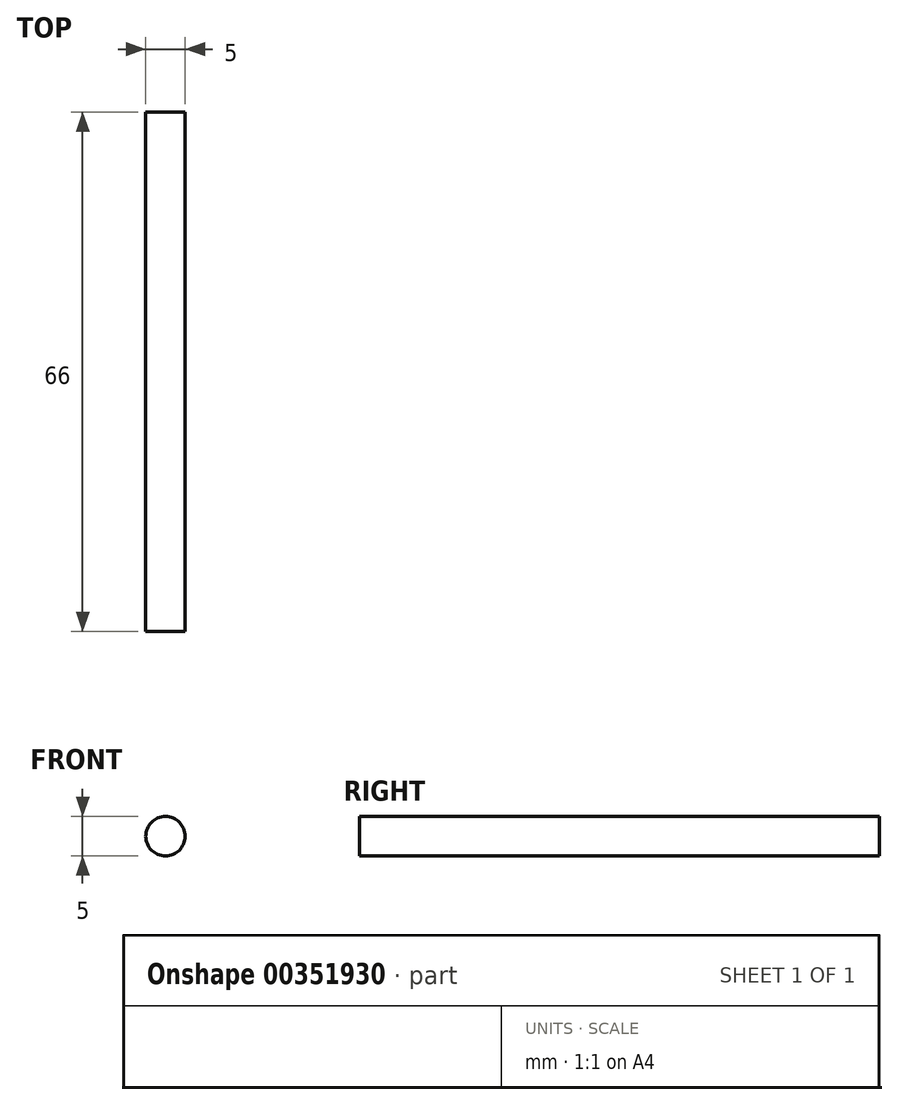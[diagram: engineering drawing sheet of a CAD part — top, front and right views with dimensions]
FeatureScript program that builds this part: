
annotation { "Feature Type Name" : "Feature", "Feature Type Description" : "" }
export const myFeature = defineFeature(function(context is Context, id is Id, definition is map)
    precondition{}
    {
        {
            var Q0;
            Q0=qCreatedBy(makeId("Front.planeOp"),FACE);
            var sketch = newSketch(context, id + "F0", { "sketchPlane" : qUnion([Q0])});
            skCircle(sketch, "E0", {"center": v(0, 0) * mm, "radius": 2.5 * mm});
            skSolve(sketch);
        }
        {
            var Q0;
            Q0 = qSketchRegion(id + "F0", true);
            extrude(context, id + "F1", {"entities" : qUnion([Q0]), "depth" : 66 * mm});
        }
    });
